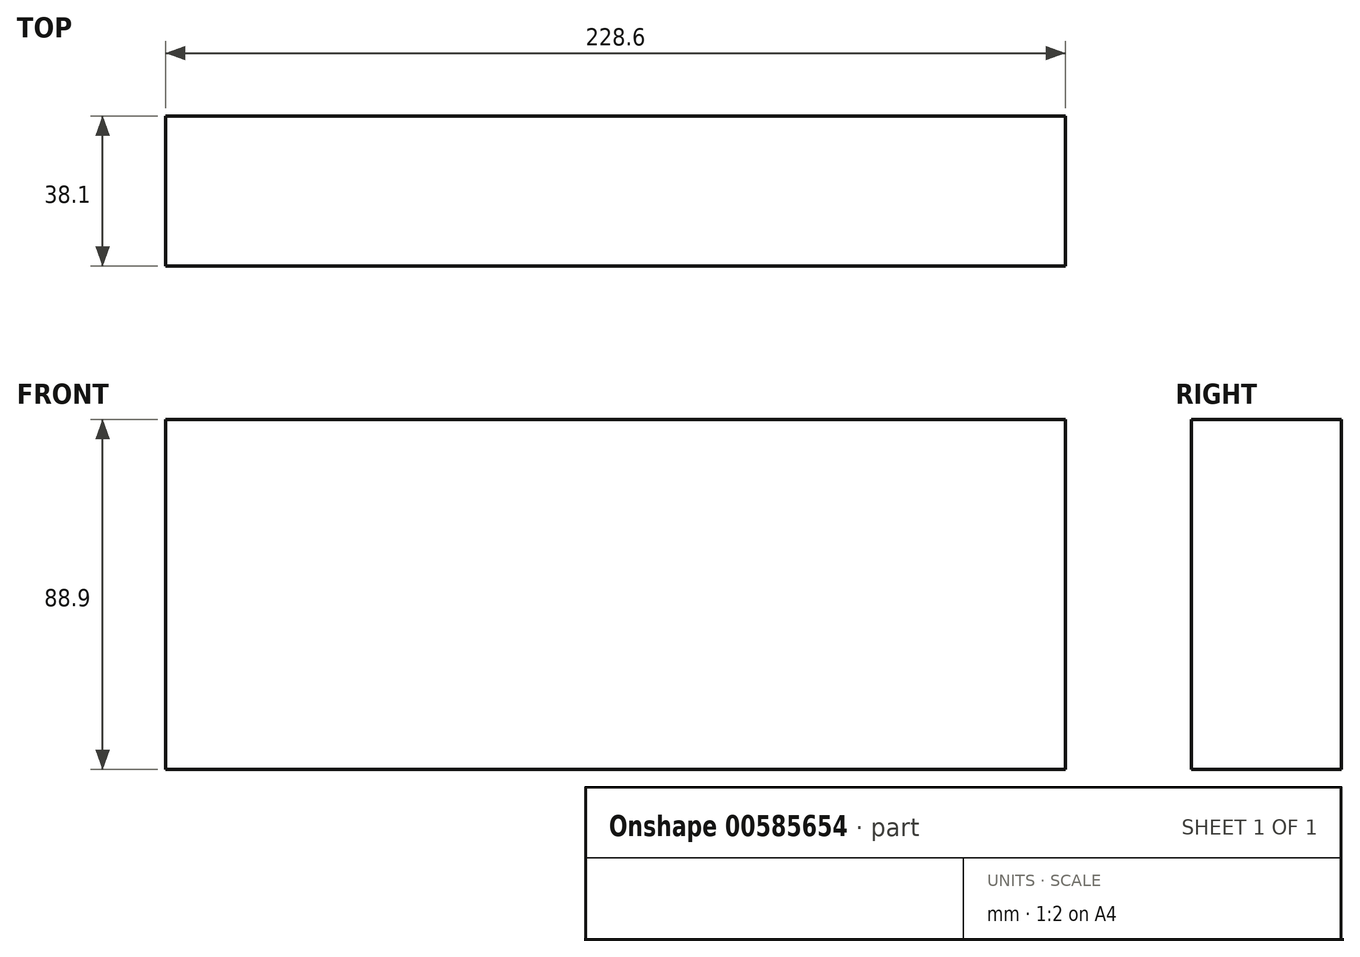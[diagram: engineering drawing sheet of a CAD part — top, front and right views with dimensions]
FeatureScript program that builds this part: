
annotation { "Feature Type Name" : "Feature", "Feature Type Description" : "" }
export const myFeature = defineFeature(function(context is Context, id is Id, definition is map)
    precondition{}
    {
        {
            var Q0;
            Q0=qCreatedBy(makeId("Right.planeOp"),FACE);
            var sketch = newSketch(context, id + "F0", { "sketchPlane" : qUnion([Q0])});
            skLineSegment(sketch, "E0.bottom", {"start": v(0, 0) * mm, "end": v(38.1, 0) * mm});
            skLineSegment(sketch, "E0.top", {"start": v(0, 88.9) * mm, "end": v(38.1, 88.9) * mm});
            skLineSegment(sketch, "E0.left", {"start": v(0, 0) * mm, "end": v(0, 88.9) * mm});
            skLineSegment(sketch, "E0.right", {"start": v(38.1, 0) * mm, "end": v(38.1, 88.9) * mm});
            skSolve(sketch);
        }
        {
            var Q0;
            Q0=qSketchRegion(id+"F0",true);
            extrude(context, id + "F1", {"entities" : qUnion([Q0]), "oppositeDirection" : true, "depth" : 228.6 * mm, "offsetDistance" : 25.4 * mm});
        }
    });
